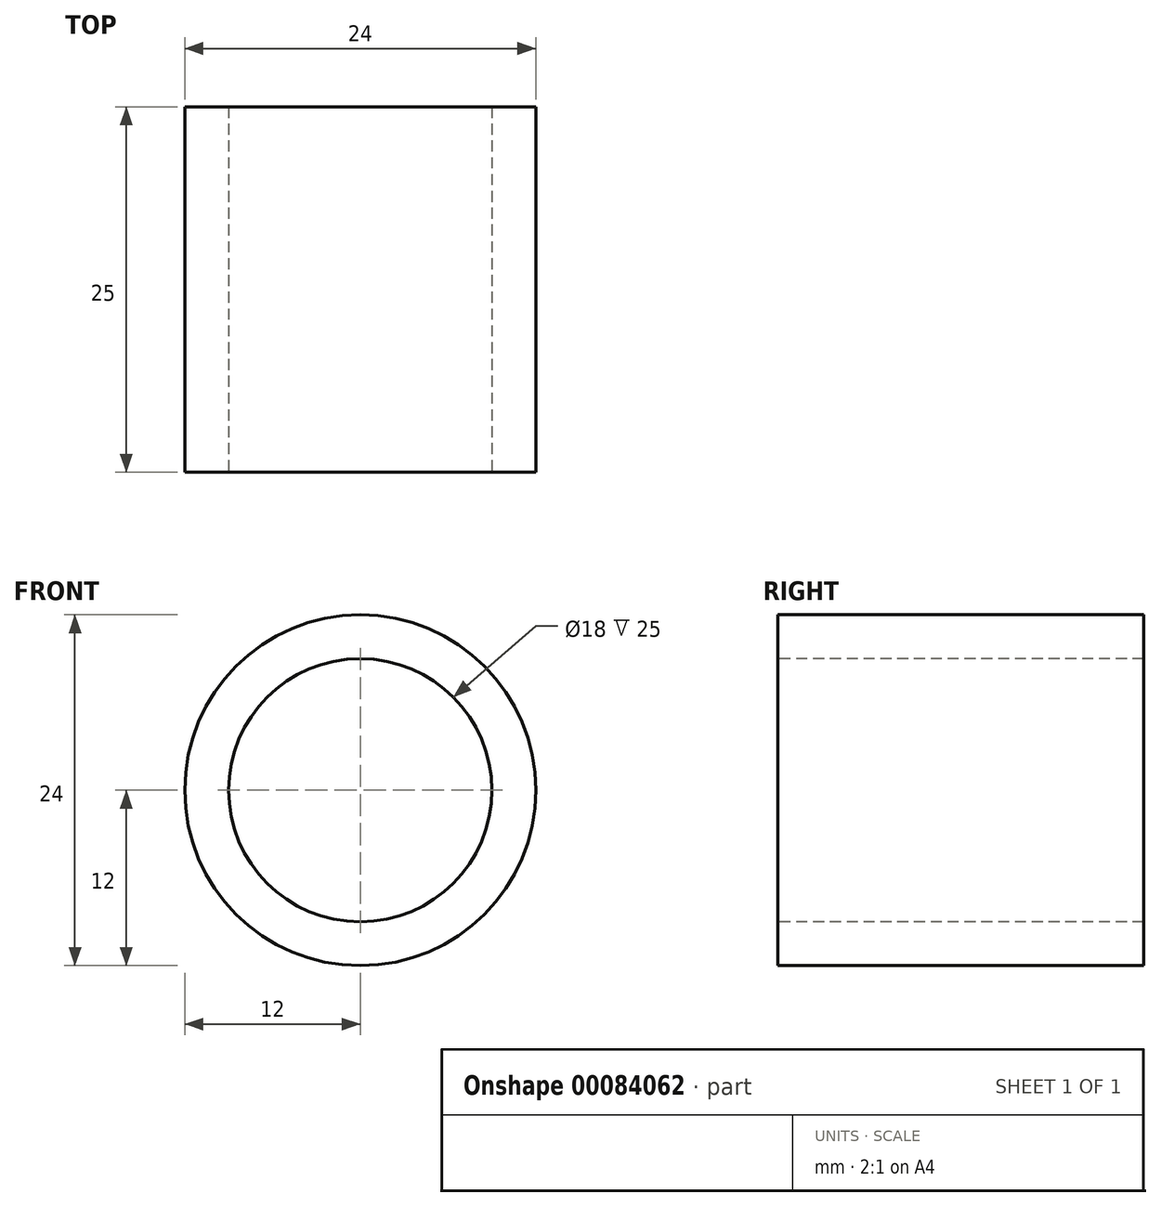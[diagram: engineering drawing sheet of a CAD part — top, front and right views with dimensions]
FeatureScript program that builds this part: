
annotation { "Feature Type Name" : "Feature", "Feature Type Description" : "" }
export const myFeature = defineFeature(function(context is Context, id is Id, definition is map)
    precondition{}
    {
        {
            var Q0;
            Q0=qCreatedBy(makeId("Front.planeOp"),FACE);
            var sketch = newSketch(context, id + "F0", { "sketchPlane" : qUnion([Q0])});
            skCircle(sketch, "E0", {"center": v(0, 0) * mm, "radius": 9 * mm});
            skCircle(sketch, "E1", {"center": v(0, 0) * mm, "radius": 12 * mm});
            skSolve(sketch);
        }
        {
            var Q0;
            Q0=makeQuery(id+"F0.imprint","IMPRINT",FACE,{"disambiguationData":[TD([[makeQuery(id+"F0.imprint","IMPRINT",EDGE,{"derivedFrom":sQuery(id+"F0.wireOp",EDGE,"E0")}),-1.0]])]});
            extrude(context, id + "F1", {"entities" : qUnion([Q0]), "oppositeDirection" : true, "depth" : 25 * mm});
        }
    });
